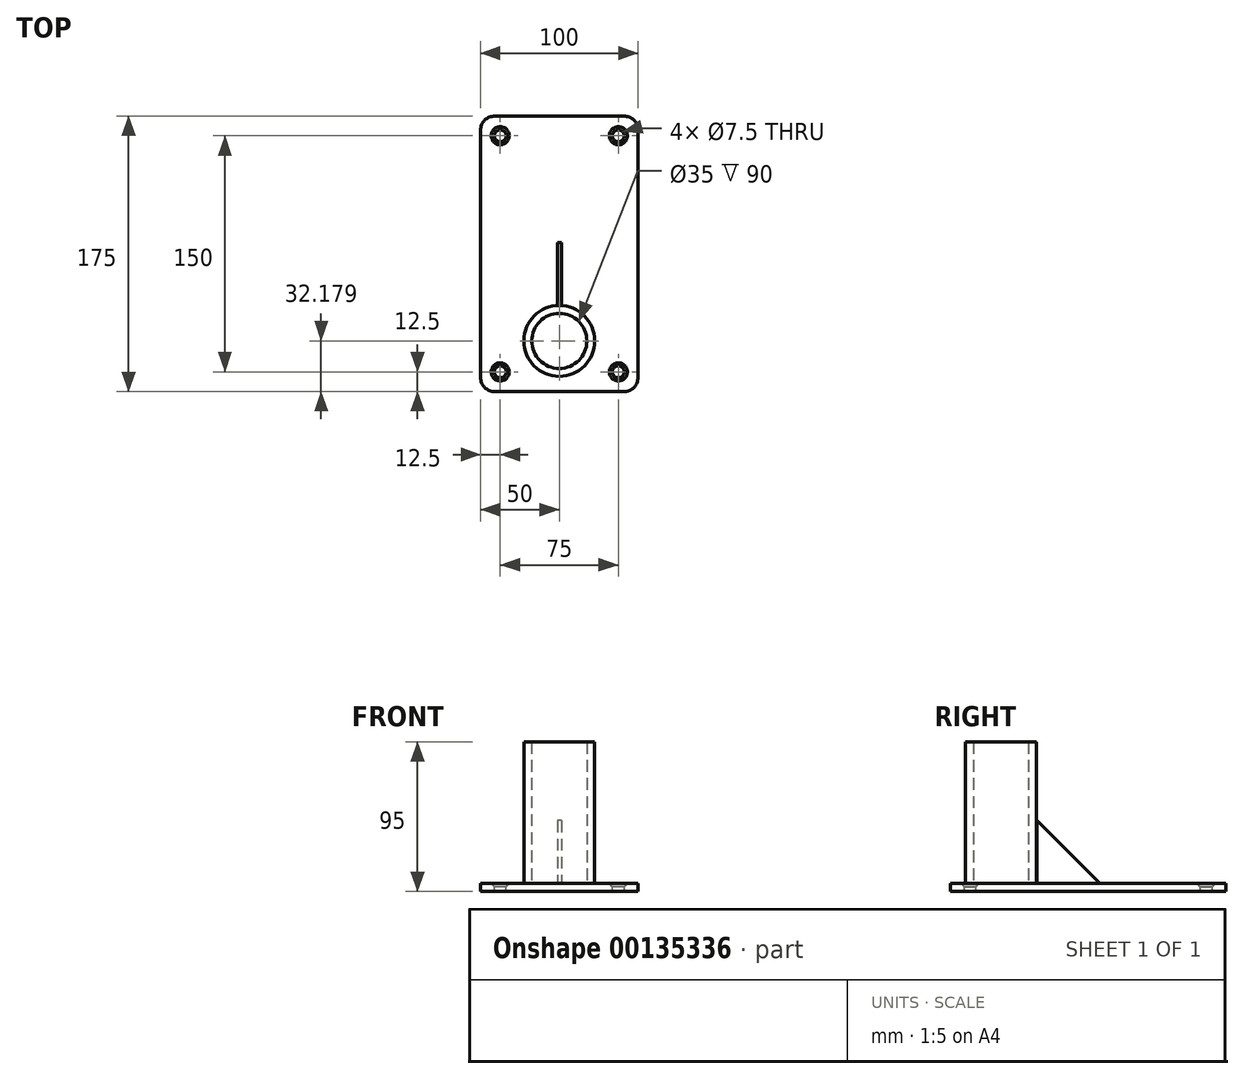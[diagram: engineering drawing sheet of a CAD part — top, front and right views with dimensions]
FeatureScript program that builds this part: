
annotation { "Feature Type Name" : "Feature", "Feature Type Description" : "" }
export const myFeature = defineFeature(function(context is Context, id is Id, definition is map)
    precondition{}
    {
        {
            var Q0;
            Q0=qCreatedBy(makeId("Top.planeOp"),FACE);
            var sketch = newSketch(context, id + "F0", { "sketchPlane" : qUnion([Q0])});
            skLineSegment(sketch, "E0.bottom", {"start": v(-41, -87.5) * mm, "end": v(41, -87.5) * mm});
            skLineSegment(sketch, "E0.top", {"start": v(-41, 87.5) * mm, "end": v(41, 87.5) * mm});
            skLineSegment(sketch, "E0.left", {"start": v(-50, -78.5) * mm, "end": v(-50, 78.5) * mm});
            skLineSegment(sketch, "E0.right", {"start": v(50, -78.5) * mm, "end": v(50, 78.5) * mm});
            skPoint(sketch, "E0.middle", {"position": v(0, 0) * mm});
            skCircle(sketch, "E1", {"center": v(0, -55.32) * mm, "radius": 22.5 * mm});
            skPoint(sketch, "E1.centerSnap0", {"position": v(0, -87.5) * mm});
            skCircle(sketch, "E2.0", {"center": v(0, -55.32) * mm, "radius": 17.5 * mm});
            skLineSegment(sketch, "E3.bottom", {"start": v(37.5, 75) * mm, "end": v(-37.5, 75) * mm, "construction": true});
            skLineSegment(sketch, "E3.top", {"start": v(37.5, -75) * mm, "end": v(-37.5, -75) * mm, "construction": true});
            skLineSegment(sketch, "E3.left", {"start": v(37.5, 75) * mm, "end": v(37.5, -75) * mm, "construction": true});
            skLineSegment(sketch, "E3.right", {"start": v(-37.5, 75) * mm, "end": v(-37.5, -75) * mm, "construction": true});
            skCircle(sketch, "E4", {"center": v(37.5, 75) * mm, "radius": 3.75 * mm});
            skCircle(sketch, "E5.MirrorC", {"center": v(37.5, -75) * mm, "radius": 3.75 * mm});
            skCircle(sketch, "E6.MirrorC", {"center": v(-37.5, 75) * mm, "radius": 3.75 * mm});
            skCircle(sketch, "E7.MirrorC", {"center": v(-37.5, -75) * mm, "radius": 3.75 * mm});
            skPoint(sketch, "E8.visualSharp", {"position": v(50, 87.5) * mm});
            skArc(sketch, "E8.filletArc", {"start": v(50, 78.5) * mm, "mid": v(47.36, 84.86) * mm, "end": v(41, 87.5) * mm});
            skPoint(sketch, "E9.visualSharp", {"position": v(50, -87.5) * mm});
            skArc(sketch, "E9.filletArc", {"start": v(41, -87.5) * mm, "mid": v(47.36, -84.86) * mm, "end": v(50, -78.5) * mm});
            skPoint(sketch, "E10.visualSharp", {"position": v(-50, -87.5) * mm});
            skArc(sketch, "E10.filletArc", {"start": v(-50, -78.5) * mm, "mid": v(-47.36, -84.86) * mm, "end": v(-41, -87.5) * mm});
            skPoint(sketch, "E11.visualSharp", {"position": v(-50, 87.5) * mm});
            skArc(sketch, "E11.filletArc", {"start": v(-41, 87.5) * mm, "mid": v(-47.36, 84.86) * mm, "end": v(-50, 78.5) * mm});
            skSolve(sketch);
        }
        {
            var Q0;
            Q0=makeQuery(id+"F0.imprint","IMPRINT",FACE,{"disambiguationData":[TD([[makeQuery(id+"F0.imprint","IMPRINT",EDGE,{"derivedFrom":sQuery(id+"F0.wireOp",EDGE,"E1")}),1.0]])]});
            extrude(context, id + "F1", {"entities" : qUnion([Q0]), "depth" : 90 * mm});
        }
        {
            var Q0;
            Q0=makeQuery(id+"F0.imprint","IMPRINT",FACE,{"disambiguationData":[TD([[makeQuery(id+"F0.imprint","IMPRINT",EDGE,{"derivedFrom":sQuery(id+"F0.wireOp",EDGE,"E0.bottom")}),1.0]])]});
            var Q1;
            Q1=makeQuery(id+"F0.imprint","IMPRINT",FACE,{"disambiguationData":[TD([[makeQuery(id+"F0.imprint","IMPRINT",EDGE,{"derivedFrom":sQuery(id+"F0.wireOp",EDGE,"E1")}),1.0]])]});
            var Q2;
            Q2=makeQuery(id+"F0.imprint","IMPRINT",FACE,{"disambiguationData":[TD([[makeQuery(id+"F0.imprint","IMPRINT",EDGE,{"derivedFrom":sQuery(id+"F0.wireOp",EDGE,"E2.0")}),1.0]])]});
            extrude(context, id + "F2", {"entities" : qUnion([Q0, Q1, Q2]), "oppositeDirection" : true, "depth" : 5 * mm});
        }
        {
            var Q0;
            Q0=qCreatedBy(makeId("Right.planeOp"),FACE);
            var sketch = newSketch(context, id + "F3", { "sketchPlane" : qUnion([Q0])});
            skLineSegment(sketch, "E12", {"start": v(-32.69, 0) * mm, "end": v(7.31, 0) * mm});
            skLineSegment(sketch, "E13", {"start": v(7.31, 0) * mm, "end": v(-32.69, 40) * mm});
            skLineSegment(sketch, "E14", {"start": v(-32.69, 40) * mm, "end": v(-32.69, 0) * mm});
            skPoint(sketch, "E15.start.orphan", {"position": v(-25.1, 0) * mm});
            skSolve(sketch);
        }
        {
            var Q0;
            Q0=makeQuery(id+"F3.imprint","IMPRINT",FACE,{"disambiguationData":[TD([[makeQuery(id+"F3.imprint","IMPRINT",EDGE,{"derivedFrom":sQuery(id+"F3.wireOp",EDGE,"E12")}),1.0]])]});
            extrude(context, id + "F4", {"entities" : qUnion([Q0]), "operationType" : NewBodyOperationType.ADD, "endBound" : BoundingType.SYMMETRIC, "depth" : 2.5 * mm});
        }
        {
            var Q0;
            Q0=makeQuery(id+"F2.opExtrude","CAP_EDGE",EDGE,{"disambiguationData":[OSD([sQuery(id+"F0.wireOp",EDGE,"E4")])],"isStart":true});
            var Q1;
            Q1=makeQuery(id+"F2.opExtrude","CAP_EDGE",EDGE,{"disambiguationData":[OSD([sQuery(id+"F0.wireOp",EDGE,"E6.MirrorC")])],"isStart":true});
            var Q2;
            Q2=makeQuery(id+"F2.opExtrude","CAP_EDGE",EDGE,{"disambiguationData":[OSD([sQuery(id+"F0.wireOp",EDGE,"E5.MirrorC")])],"isStart":true});
            var Q3;
            Q3=makeQuery(id+"F2.opExtrude","CAP_EDGE",EDGE,{"disambiguationData":[OSD([sQuery(id+"F0.wireOp",EDGE,"E7.MirrorC")])],"isStart":true});
            chamfer(context, id + "F5", {"entities" : qUnion([Q0, Q1, Q2, Q3]), "width" : 2 * mm, "tangentPropagation" : true});
        }
    });
